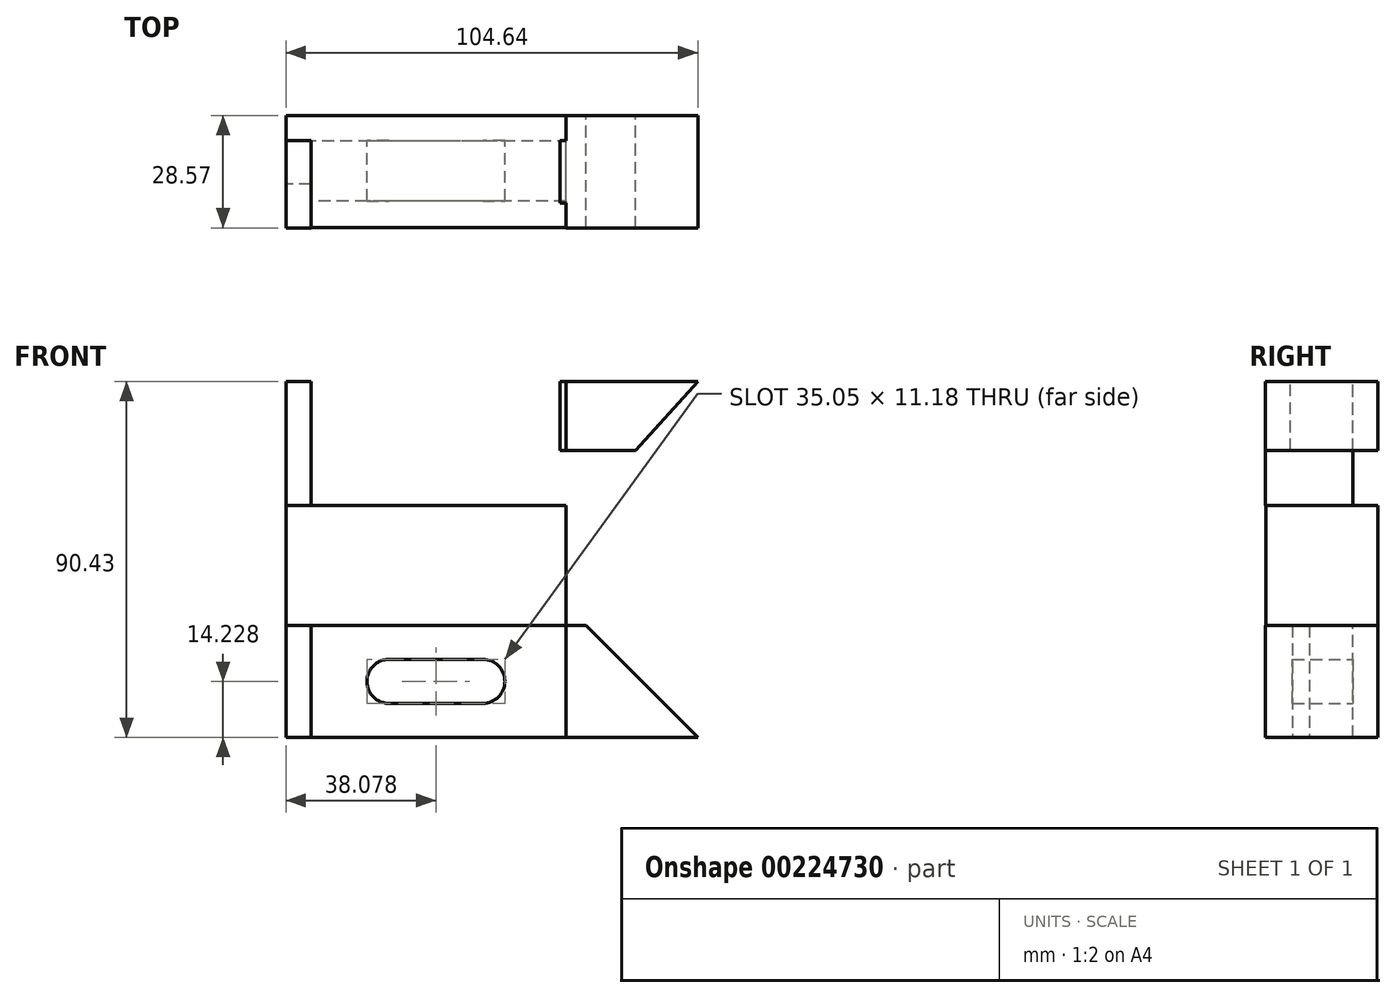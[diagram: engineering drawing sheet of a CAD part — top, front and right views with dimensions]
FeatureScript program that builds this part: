
annotation { "Feature Type Name" : "Feature", "Feature Type Description" : "" }
export const myFeature = defineFeature(function(context is Context, id is Id, definition is map)
    precondition{}
    {
        {
            var Q0;
            Q0=qCreatedBy(makeId("Front.planeOp"),FACE);
            var sketch = newSketch(context, id + "F0", { "sketchPlane" : qUnion([Q0])});
            skLineSegment(sketch, "E0.bottom", {"start": v(-81.31, 22.72) * mm, "end": v(-10.2, 22.72) * mm});
            skLineSegment(sketch, "E0.top", {"start": v(-81.31, -7.76) * mm, "end": v(-10.2, -7.76) * mm});
            skLineSegment(sketch, "E0.left", {"start": v(-81.31, 22.72) * mm, "end": v(-81.31, -7.76) * mm});
            skLineSegment(sketch, "E0.right", {"start": v(-10.2, 22.72) * mm, "end": v(-10.2, -7.76) * mm});
            skLineSegment(sketch, "E1.bottom", {"start": v(-81.31, 22.72) * mm, "end": v(-5.12, 22.72) * mm});
            skLineSegment(sketch, "E1.top", {"start": v(-81.31, 54.22) * mm, "end": v(-5.12, 54.22) * mm});
            skLineSegment(sketch, "E1.left", {"start": v(-81.31, 22.72) * mm, "end": v(-81.31, 54.22) * mm});
            skLineSegment(sketch, "E2.bottom", {"start": v(-81.31, -7.76) * mm, "end": v(-5.12, -7.76) * mm});
            skLineSegment(sketch, "E2.top", {"start": v(-81.31, -36.2) * mm, "end": v(-5.12, -36.2) * mm});
            skLineSegment(sketch, "E2.left", {"start": v(-81.31, -7.76) * mm, "end": v(-81.31, -36.2) * mm});
            skLineSegment(sketch, "E3", {"start": v(-5.12, 54.22) * mm, "end": v(23.33, 54.22) * mm});
            skLineSegment(sketch, "E4", {"start": v(-5.12, 22.72) * mm, "end": v(23.33, 54.22) * mm});
            skLineSegment(sketch, "E5", {"start": v(-11.72, 36.7) * mm, "end": v(-11.72, 54.22) * mm});
            skLineSegment(sketch, "E6", {"start": v(-11.72, 54.22) * mm, "end": v(-11.72, 36.7) * mm});
            skLineSegment(sketch, "E7", {"start": v(-11.72, -18.68) * mm, "end": v(-11.72, -36.2) * mm});
            skPoint(sketch, "E8.positionSnap0", {"position": v(-43.22, -36.2) * mm});
            skPoint(sketch, "E9.start.orphan", {"position": v(-81.31, 38.47) * mm});
            skPoint(sketch, "E10.start.orphan", {"position": v(-81.31, -21.98) * mm});
            skLineSegment(sketch, "E11.bottom", {"start": v(-55.14, -27.57) * mm, "end": v(-31.27, -27.57) * mm});
            skLineSegment(sketch, "E11.top", {"start": v(-55.17, -16.4) * mm, "end": v(-31.3, -16.4) * mm});
            skPoint(sketch, "E11.middle", {"position": v(-43.22, -21.98) * mm});
            skArc(sketch, "E12", {"start": v(-55.17, -16.4) * mm, "mid": v(-60.76, -22) * mm, "end": v(-55.14, -27.57) * mm});
            skArc(sketch, "E13", {"start": v(-31.27, -27.57) * mm, "mid": v(-25.7, -21.97) * mm, "end": v(-31.3, -16.4) * mm});
            skLineSegment(sketch, "E14.bottom", {"start": v(-55.13, 44.06) * mm, "end": v(-31.25, 44.06) * mm});
            skLineSegment(sketch, "E14.top", {"start": v(-55.19, 32.88) * mm, "end": v(-31.3, 32.88) * mm});
            skPoint(sketch, "E14.middle", {"position": v(-43.22, 38.47) * mm});
            skPoint(sketch, "E14.middle.positionSnap0", {"position": v(-43.22, 54.22) * mm});
            skPoint(sketch, "E14.centerSnap0", {"position": v(-43.22, 54.22) * mm});
            skArc(sketch, "E15", {"start": v(-55.13, 44.06) * mm, "mid": v(-60.77, 38.5) * mm, "end": v(-55.19, 32.88) * mm});
            skArc(sketch, "E16", {"start": v(-31.3, 32.88) * mm, "mid": v(-25.72, 38.44) * mm, "end": v(-31.25, 44.06) * mm});
            skLineSegment(sketch, "E17", {"start": v(-5.12, -36.2) * mm, "end": v(23.33, -36.2) * mm});
            skPoint(sketch, "E18.orphan", {"position": v(23.33, -48.06) * mm});
            skLineSegment(sketch, "E19", {"start": v(-11.72, 36.7) * mm, "end": v(7.5, 36.7) * mm});
            skLineSegment(sketch, "E20", {"start": v(-5.12, -7.76) * mm, "end": v(23.33, -36.2) * mm});
            skLineSegment(sketch, "E21", {"start": v(-11.72, -18.68) * mm, "end": v(5.8, -18.68) * mm});
            skLineSegment(sketch, "E22", {"start": v(-74.96, 22.72) * mm, "end": v(-74.96, 54.22) * mm});
            skLineSegment(sketch, "E23", {"start": v(-74.96, -7.76) * mm, "end": v(-74.96, -36.2) * mm});
            skSolve(sketch);
        }
        {
            var Q0;
            {var subQ0=sQuery(id+"F0.wireOp",EDGE,"E1.left");Q0=makeQuery(id+"F0.imprint","IMPRINT",FACE,{"disambiguationData":[TD([[makeQuery(id+"F0.imprint","IMPRINT",EDGE,{"derivedFrom":subQ0}),-1.0]])]});}
            var Q1;
            {var subQ1=sQuery(id+"F0.wireOp",EDGE,"E6");Q1=makeQuery(id+"F0.imprint","IMPRINT",FACE,{"disambiguationData":[TD([[makeQuery(id+"F0.imprint","IMPRINT",EDGE,{"derivedFrom":subQ1}),-1.0]])]});}
            var Q2;
            {var subQ1=sQuery(id+"F0.wireOp",EDGE,"E3");Q2=makeQuery(id+"F0.imprint","IMPRINT",FACE,{"disambiguationData":[TD([[makeQuery(id+"F0.imprint","IMPRINT",EDGE,{"derivedFrom":subQ1}),-1.0]])]});}
            extrude(context, id + "F1", {"entities" : qUnion([Q0, Q1, Q2]), "depth" : 28.57 * mm});
        }
        {
            var Q0;
            {var subQ6=sQuery(id+"F0.wireOp",EDGE,"E7");Q0=makeQuery(id+"F0.imprint","IMPRINT",FACE,{"disambiguationData":[TD([[makeQuery(id+"F0.imprint","IMPRINT",EDGE,{"derivedFrom":subQ6}),-1.0]])]});}
            var Q1;
            {var subQ3=sQuery(id+"F0.wireOp",EDGE,"E7");Q1=makeQuery(id+"F0.imprint","IMPRINT",FACE,{"disambiguationData":[TD([[makeQuery(id+"F0.imprint","IMPRINT",EDGE,{"derivedFrom":subQ3}),1.0]])]});}
            var Q2;
            {var subQ0=sQuery(id+"F0.wireOp",EDGE,"E2.left");Q2=makeQuery(id+"F0.imprint","IMPRINT",FACE,{"disambiguationData":[TD([[makeQuery(id+"F0.imprint","IMPRINT",EDGE,{"derivedFrom":subQ0}),1.0]])]});}
            extrude(context, id + "F2", {"entities" : qUnion([Q0, Q1, Q2]), "depth" : 28.57 * mm});
        }
        {
            var Q0;
            Q0=makeQuery(id+"F1.opExtrude","SWEPT_FACE",FACE,{"disambiguationData":[OSD([sQuery(id+"F0.wireOp",EDGE,"E1.top"),sQuery(id+"F0.wireOp",EDGE,"E3")])]});
            var sketch = newSketch(context, id + "F3", { "sketchPlane" : qUnion([Q0])});
            skLineSegment(sketch, "E24.bottom", {"start": v(-74.96, -22.23) * mm, "end": v(-10.2, -22.23) * mm});
            skLineSegment(sketch, "E24.top", {"start": v(-81.31, -28.58) * mm, "end": v(-10.2, -28.58) * mm});
            skLineSegment(sketch, "E24.left", {"start": v(-81.31, -22.23) * mm, "end": v(-81.31, -28.58) * mm});
            skLineSegment(sketch, "E24.right", {"start": v(-10.2, -22.23) * mm, "end": v(-10.2, -28.58) * mm});
            skLineSegment(sketch, "E25.bottom", {"start": v(-81.31, 0) * mm, "end": v(-10.2, 0) * mm});
            skLineSegment(sketch, "E25.top", {"start": v(-81.31, -6.35) * mm, "end": v(-10.2, -6.35) * mm});
            skLineSegment(sketch, "E25.left", {"start": v(-81.31, 0) * mm, "end": v(-81.31, -6.35) * mm});
            skLineSegment(sketch, "E25.right", {"start": v(-10.2, 0) * mm, "end": v(-10.2, -6.35) * mm});
            skLineSegment(sketch, "E26", {"start": v(-81.31, -22.23) * mm, "end": v(-81.31, -17.35) * mm});
            skLineSegment(sketch, "E27", {"start": v(-81.31, -17.35) * mm, "end": v(-74.96, -17.35) * mm});
            skLineSegment(sketch, "E28", {"start": v(-74.96, -17.35) * mm, "end": v(-74.96, -22.23) * mm});
            skSolve(sketch);
        }
        {
            var Q0;
            Q0=makeQuery(id+"F3.imprint","IMPRINT",FACE,{"disambiguationData":[TD([[makeQuery(id+"F3.imprint","IMPRINT",EDGE,{"derivedFrom":sQuery(id+"F3.wireOp",EDGE,"E25.bottom")}),-1.0]])]});
            var Q1;
            Q1=makeQuery(id+"F3.imprint","IMPRINT",FACE,{"disambiguationData":[TD([[makeQuery(id+"F3.imprint","IMPRINT",EDGE,{"derivedFrom":sQuery(id+"F3.wireOp",EDGE,"E24.bottom")}),-1.0]])]});
            extrude(context, id + "F4", {"entities" : qUnion([Q0, Q1]), "operationType" : NewBodyOperationType.REMOVE, "endBound" : BoundingType.THROUGH_ALL, "oppositeDirection" : true, "depth" : 25.4 * mm});
        }
        {
            var Q0;
            Q0=makeQuery(id+"F2.opExtrude","SWEPT_FACE",FACE,{"disambiguationData":[OSD([sQuery(id+"F0.wireOp",EDGE,"E2.top"),sQuery(id+"F0.wireOp",EDGE,"E17")])]});
            var sketch = newSketch(context, id + "F5", { "sketchPlane" : qUnion([Q0])});
            skLineSegment(sketch, "E29.bottom", {"start": v(-81.45, 6.28) * mm, "end": v(-10.33, 6.28) * mm});
            skLineSegment(sketch, "E29.top", {"start": v(-81.45, -0.07) * mm, "end": v(-10.33, -0.07) * mm});
            skLineSegment(sketch, "E29.left", {"start": v(-81.45, 6.28) * mm, "end": v(-81.45, -0.07) * mm});
            skLineSegment(sketch, "E29.right", {"start": v(-10.33, 6.28) * mm, "end": v(-10.33, -0.07) * mm});
            skSolve(sketch);
        }
        {
            var Q0;
            {var subQ0=sQuery(id+"F5.wireOp",EDGE,"3c813544-626e-4872-b0b1-93bcd080724c");Q0=makeQuery(id+"F5.imprint","IMPRINT",FACE,{"disambiguationData":[TD([[makeQuery(id+"F5.imprint","IMPRINT",EDGE,{"derivedFrom":subQ0}),-1.0]])]});}
            var Q1;
            {var subQ1=sQuery(id+"F5.wireOp",EDGE,"E29.top");Q1=makeQuery(id+"F5.imprint","IMPRINT",FACE,{"disambiguationData":[TD([[makeQuery(id+"F5.imprint","IMPRINT",EDGE,{"derivedFrom":subQ1}),1.0]])]});}
            var Q2;
            {var subQ1=sQuery(id+"F5.wireOp",EDGE,"a812d382-311a-4a4d-8179-64caee7b3d42.bottom");Q2=makeQuery(id+"F5.imprint","IMPRINT",FACE,{"disambiguationData":[TD([[makeQuery(id+"F5.imprint","IMPRINT",EDGE,{"derivedFrom":subQ1}),-1.0]])]});}
            var Q3;
            {var subQ0=sQuery(id+"F5.wireOp",EDGE,"E29.right");var subQ1=sQuery(id+"F5.wireOp",EDGE,"E29.bottom");var subQ2=makeQuery(id+"F5.imprint","INTERSECT",VERTEX,{"derivedFrom":[subQ1,subQ0]});Q3=makeQuery(id+"F5.imprint","IMPRINT",FACE,{"disambiguationData":[TD([[makeQuery(id+"F5.imprint","IMPRINT",EDGE,{"disambiguationData":[TD([[subQ2,1.0]])],"derivedFrom":subQ1}),-1.0]])]});}
            extrude(context, id + "F6", {"entities" : qUnion([Q0, Q1, Q2, Q3]), "operationType" : NewBodyOperationType.REMOVE, "endBound" : BoundingType.THROUGH_ALL, "oppositeDirection" : true, "depth" : 25.4 * mm});
        }
        {
            var Q0;
            Q0=makeQuery(id+"F2.opExtrude","SWEPT_FACE",FACE,{"disambiguationData":[OSD([sQuery(id+"F0.wireOp",EDGE,"E2.left")])]});
            var sketch = newSketch(context, id + "F7", { "sketchPlane" : qUnion([Q0])});
            skLineSegment(sketch, "E30.bottom", {"start": v(17.43, -7.76) * mm, "end": v(21.68, -7.76) * mm});
            skLineSegment(sketch, "E30.top", {"start": v(17.43, -36.2) * mm, "end": v(21.68, -36.2) * mm});
            skLineSegment(sketch, "E30.left", {"start": v(17.43, -7.76) * mm, "end": v(17.43, -36.2) * mm});
            skLineSegment(sketch, "E30.right", {"start": v(21.68, -7.76) * mm, "end": v(21.68, -36.2) * mm});
            skSolve(sketch);
        }
        {
            var Q0;
            Q0=makeQuery(id+"F7.imprint","IMPRINT",FACE,{"disambiguationData":[TD([[makeQuery(id+"F7.imprint","IMPRINT",EDGE,{"derivedFrom":sQuery(id+"F7.wireOp",EDGE,"E30.bottom")}),1.0]])]});
            extrude(context, id + "F8", {"entities" : qUnion([Q0]), "operationType" : NewBodyOperationType.REMOVE, "oppositeDirection" : true, "depth" : 6.35 * mm});
        }
        {
            var Q0;
            {var subQ2=sQuery(id+"F0.wireOp",EDGE,"E2.left");Q0=makeQuery(id+"F8.boolean.opBoolean","SPLIT",FACE,{"disambiguationData":[TD([makeQuery(id+"F8.opExtrude","SWEPT_FACE",FACE,{"disambiguationData":[OSD([sQuery(id+"F7.wireOp",EDGE,"E30.right")])]})])],"derivedFrom":makeQuery(id+"F2.opExtrude","SWEPT_FACE",FACE,{"disambiguationData":[OSD([subQ2])]})});}
            extrude(context, id + "F9", {"entities" : qUnion([Q0]), "operationType" : NewBodyOperationType.REMOVE, "oppositeDirection" : true, "depth" : 71.12 * mm});
        }
        {
            var Q0;
            {var subQ5=sQuery(id+"F0.wireOp",EDGE,"E0.left");Q0=makeQuery(id+"F0.imprint","IMPRINT",FACE,{"disambiguationData":[TD([[makeQuery(id+"F0.imprint","IMPRINT",EDGE,{"derivedFrom":subQ5}),1.0]])]});}
            extrude(context, id + "F10", {"entities" : qUnion([Q0]), "depth" : 28.45 * mm});
        }
    });
